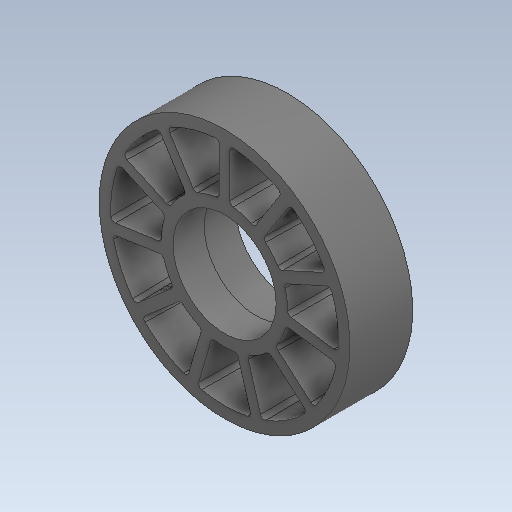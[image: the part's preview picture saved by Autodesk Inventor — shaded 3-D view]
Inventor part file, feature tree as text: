
AUTODESK INVENTOR PART (.ipt)
format: ipt  version: 2020.2 (Build 242310000, 310)  size: 379,904 bytes
history: native  units: in
note: dims shown in document units (in); Inventor stores cm internally (conversion verified against a paired STEP export)
features: fillet x1
ambient origin geometry x8: Origin, YZ Plane, XZ Plane, XY Plane, X Axis, Y Axis, Z Axis, Center Point
bodies: Solid1 (feature_tree)
feature tree (1):
  fillet  "Fillet1"  [1 undecoded]
note: 1 required parameter value undecoded (feature->parameter linkage not recoverable at this tier; creation-order binding heuristic only, values carry confidence <= 0.55)
